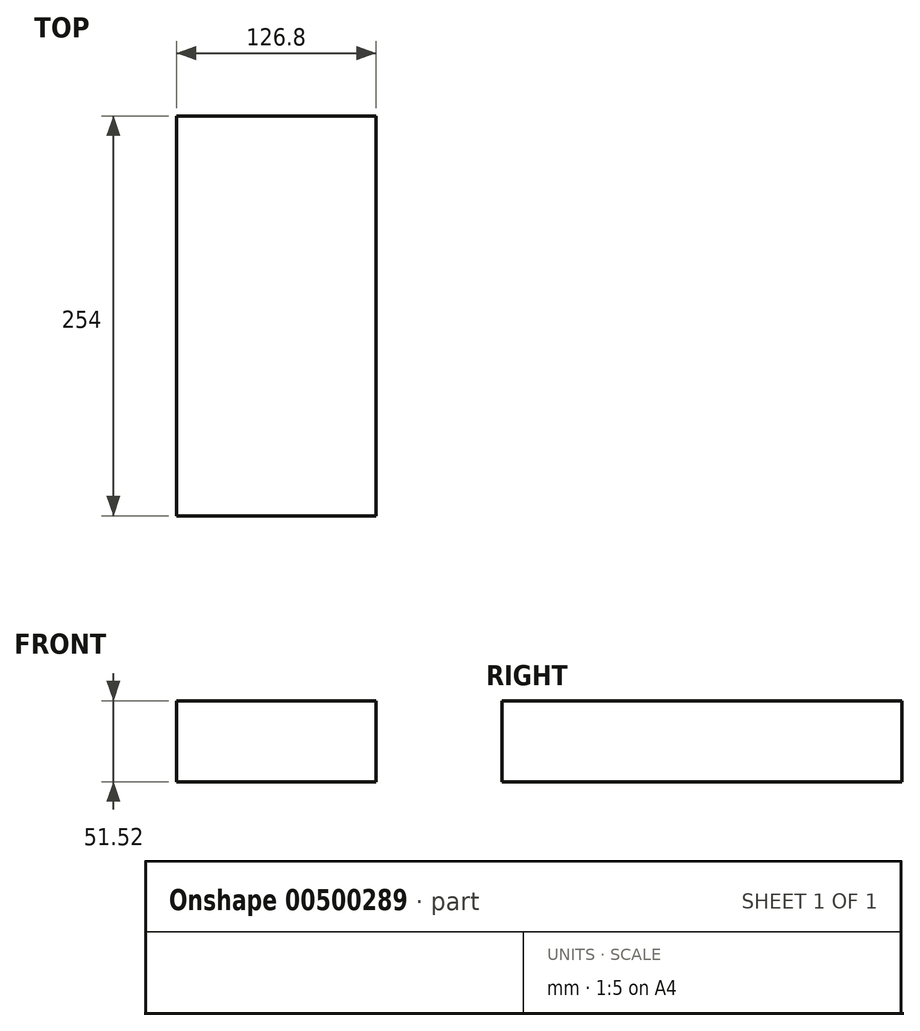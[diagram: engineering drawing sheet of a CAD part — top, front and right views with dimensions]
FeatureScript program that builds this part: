
annotation { "Feature Type Name" : "Feature", "Feature Type Description" : "" }
export const myFeature = defineFeature(function(context is Context, id is Id, definition is map)
    precondition{}
    {
        {
            var Q0;
            Q0=qCreatedBy(makeId("Front.planeOp"),FACE);
            var sketch = newSketch(context, id + "F0", { "sketchPlane" : qUnion([Q0])});
            skLineSegment(sketch, "E0.bottom", {"start": v(-63.4, 25.76) * mm, "end": v(63.4, 25.76) * mm});
            skLineSegment(sketch, "E0.top", {"start": v(-63.4, -25.76) * mm, "end": v(63.4, -25.76) * mm});
            skLineSegment(sketch, "E0.left", {"start": v(-63.4, 25.76) * mm, "end": v(-63.4, -25.76) * mm});
            skLineSegment(sketch, "E0.right", {"start": v(63.4, 25.76) * mm, "end": v(63.4, -25.76) * mm});
            skPoint(sketch, "E0.middle", {"position": v(0, 0) * mm});
            skSolve(sketch);
        }
        {
            var Q0;
            Q0=makeQuery(id+"F0.imprint","IMPRINT",FACE,{"disambiguationData":[TD([[makeQuery(id+"F0.imprint","IMPRINT",EDGE,{"derivedFrom":sQuery(id+"F0.wireOp",EDGE,"E0.bottom")}),-1.0]])]});
            extrude(context, id + "F1", {"entities" : qUnion([Q0]), "depth" : 254 * mm});
        }
    });
